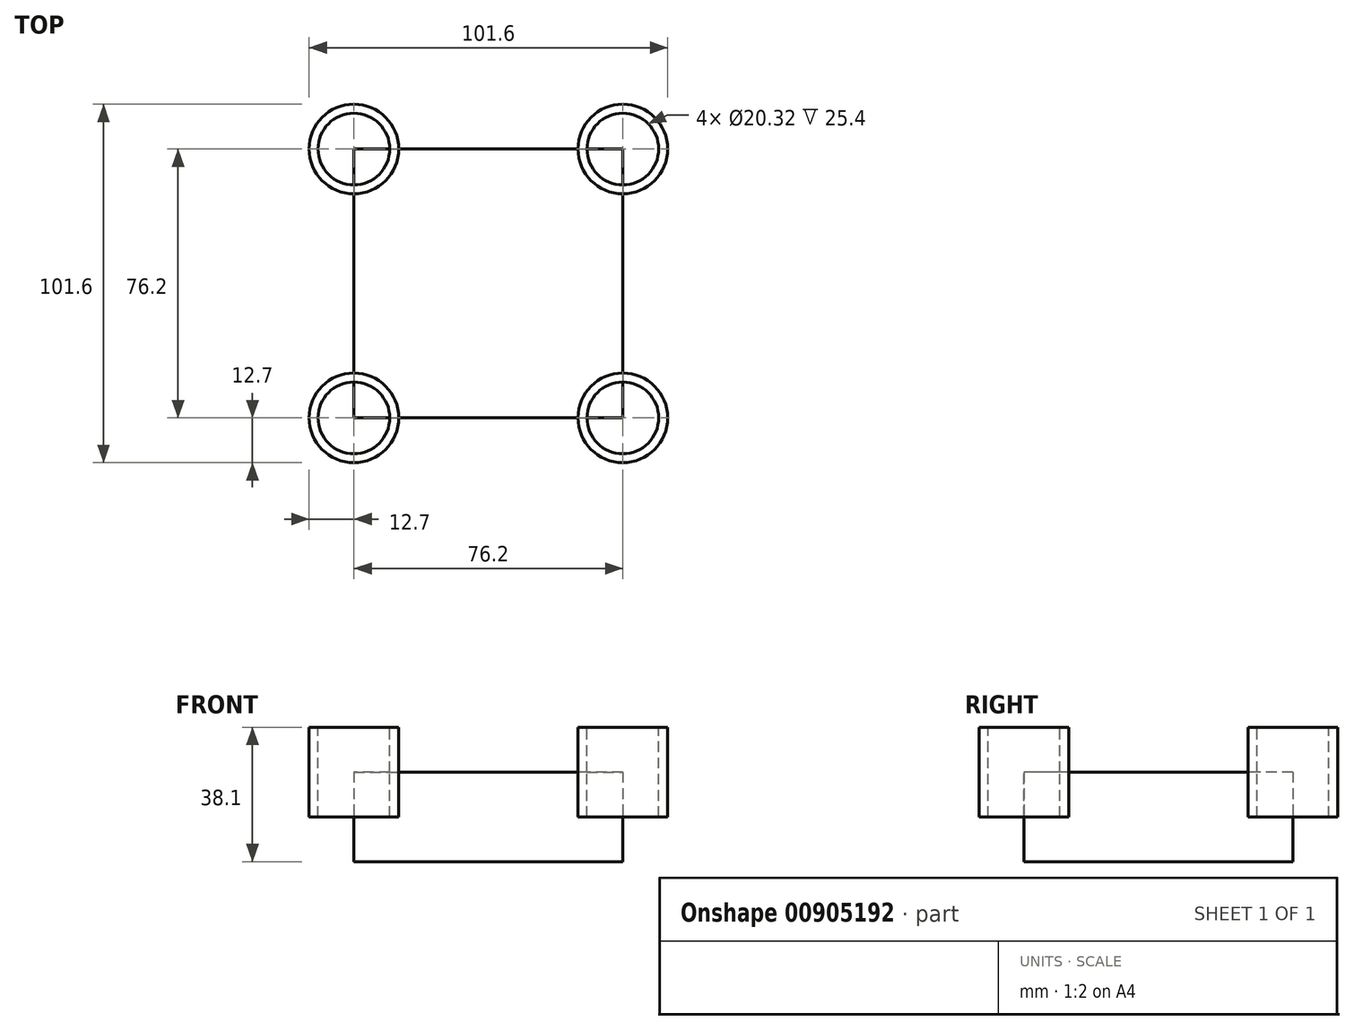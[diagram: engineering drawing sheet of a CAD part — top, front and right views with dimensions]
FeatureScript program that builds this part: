
annotation { "Feature Type Name" : "Feature", "Feature Type Description" : "" }
export const myFeature = defineFeature(function(context is Context, id is Id, definition is map)
    precondition{}
    {
        {
            var Q0;
            Q0=qCreatedBy(makeId("Top.planeOp"),FACE);
            var sketch = newSketch(context, id + "F0", { "sketchPlane" : qUnion([Q0])});
            skLineSegment(sketch, "E0.bottom", {"start": v(-38.1, 38.1) * mm, "end": v(38.1, 38.1) * mm});
            skLineSegment(sketch, "E0.top", {"start": v(-38.1, -38.1) * mm, "end": v(38.1, -38.1) * mm});
            skLineSegment(sketch, "E0.left", {"start": v(-38.1, 38.1) * mm, "end": v(-38.1, -38.1) * mm});
            skLineSegment(sketch, "E0.right", {"start": v(38.1, 38.1) * mm, "end": v(38.1, -38.1) * mm});
            skLineSegment(sketch, "E1", {"start": v(-38.1, 0) * mm, "end": v(38.1, 0) * mm, "construction": true});
            skSolve(sketch);
        }
        {
            var Q0;
            Q0=makeQuery(id+"F0.imprint","IMPRINT",FACE,{"disambiguationData":[TD([[makeQuery(id+"F0.imprint","IMPRINT",EDGE,{"derivedFrom":sQuery(id+"F0.wireOp",EDGE,"E0.bottom")}),-1.0]])]});
            extrude(context, id + "F1", {"entities" : qUnion([Q0]), "depth" : 25.4 * mm, "offsetDistance" : 25.4 * mm});
        }
        {
            var Q0;
            Q0=makeQuery(id+"F1.opExtrude","CAP_FACE",FACE,{"disambiguationData":[OSD([sQuery(id+"F0.wireOp",EDGE,"E0.bottom"),sQuery(id+"F0.wireOp",EDGE,"E0.top"),sQuery(id+"F0.wireOp",EDGE,"E0.left"),sQuery(id+"F0.wireOp",EDGE,"E0.right")])],"isStart":false});
            var sketch = newSketch(context, id + "F2", { "sketchPlane" : qUnion([Q0])});
            skCircle(sketch, "E2", {"center": v(-38.1, 38.1) * mm, "radius": 12.7 * mm});
            skLineSegment(sketch, "E3", {"start": v(0, 38.1) * mm, "end": v(0, -38.1) * mm, "construction": true});
            skLineSegment(sketch, "E4", {"start": v(-38.1, 0) * mm, "end": v(38.1, 0) * mm, "construction": true});
            skCircle(sketch, "E5", {"center": v(-38.1, 38.1) * mm, "radius": 10.16 * mm});
            skCircle(sketch, "E6.MirrorC", {"center": v(38.1, 38.1) * mm, "radius": 12.7 * mm});
            skCircle(sketch, "E7.MirrorC", {"center": v(38.1, 38.1) * mm, "radius": 10.16 * mm});
            skCircle(sketch, "E8.MirrorC", {"center": v(-38.1, -38.1) * mm, "radius": 10.16 * mm});
            skCircle(sketch, "E9.MirrorC", {"center": v(-38.1, -38.1) * mm, "radius": 12.7 * mm});
            skCircle(sketch, "E10.MirrorC", {"center": v(38.1, -38.1) * mm, "radius": 12.7 * mm});
            skCircle(sketch, "E11.MirrorC", {"center": v(38.1, -38.1) * mm, "radius": 10.16 * mm});
            skSolve(sketch);
        }
        {
            var Q0;
            Q0 = qSketchRegion(id + "F2", true);
            extrude(context, id + "F3", {"entities" : qUnion([Q0]), "operationType" : NewBodyOperationType.ADD, "endBound" : BoundingType.SYMMETRIC, "oppositeDirection" : true, "depth" : 25.4 * mm, "offsetDistance" : 25.4 * mm});
        }
    });
